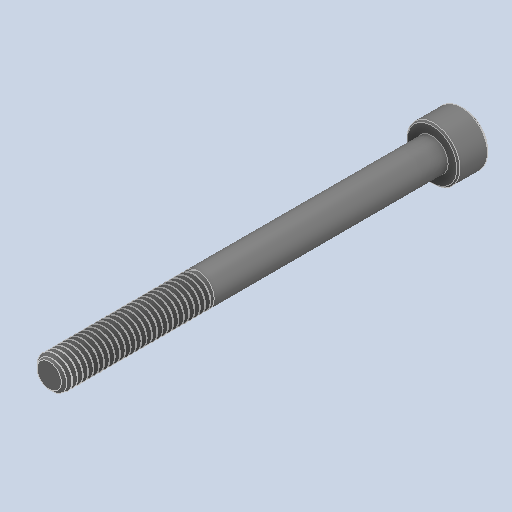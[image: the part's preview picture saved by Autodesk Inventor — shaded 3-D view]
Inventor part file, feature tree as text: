
AUTODESK INVENTOR PART (.ipt)
format: ipt  version: 2024.2 (Build 282272000, 272)  size: 671,232 bytes
history: native  units: in
note: dims shown in document units (in); Inventor stores cm internally (conversion verified against a paired STEP export)
features: chamfer x1
ambient origin geometry x8: Origin, YZ Plane, XZ Plane, XY Plane, X Axis, Y Axis, Z Axis, Center Point
bodies: Solid1 (feature_tree)
feature tree (1):
  chamfer  "Chamfer2"  [1 undecoded]
note: 1 required parameter value undecoded (feature->parameter linkage not recoverable at this tier; creation-order binding heuristic only, values carry confidence <= 0.55)
